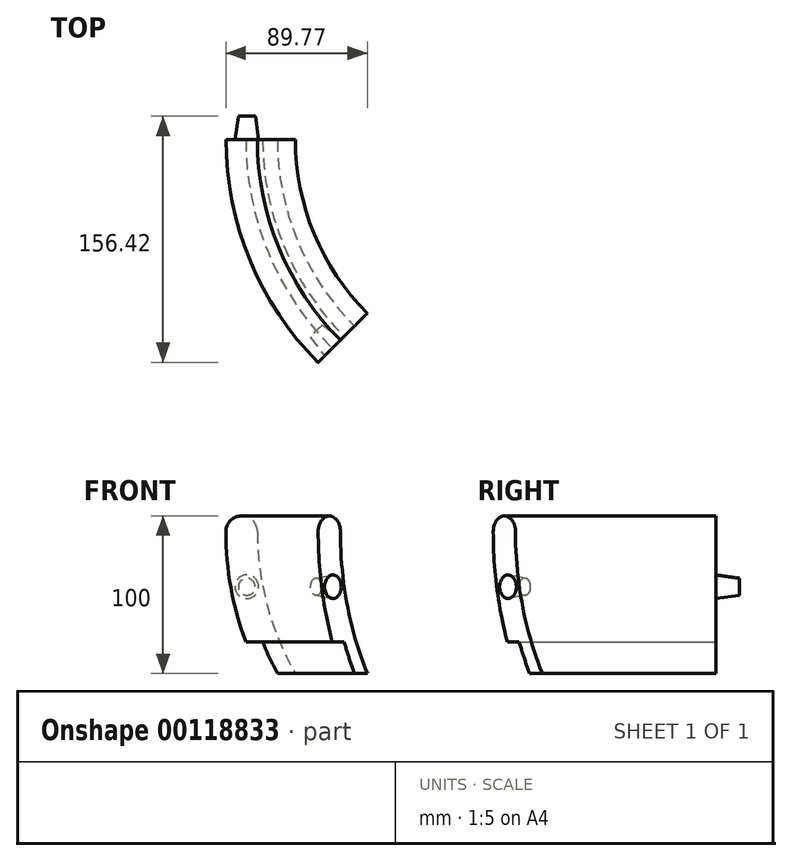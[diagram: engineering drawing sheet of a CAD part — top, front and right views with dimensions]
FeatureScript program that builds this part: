
annotation { "Feature Type Name" : "Feature", "Feature Type Description" : "" }
export const myFeature = defineFeature(function(context is Context, id is Id, definition is map)
    precondition{}
    {
        {
            var Q0;
            Q0=qCreatedBy(makeId("Front.planeOp"),FACE);
            var sketch = newSketch(context, id + "F0", { "sketchPlane" : qUnion([Q0])});
            skArc(sketch, "E0", {"start": v(-72.68, -46.84) * mm, "mid": v(-69.5, -82.4) * mm, "end": v(-60.03, -116.84) * mm});
            skLineSegment(sketch, "E1", {"start": v(127.32, -126.84) * mm, "end": v(127.32, -46.84) * mm});
            skLineSegment(sketch, "E2", {"start": v(127.32, -46.84) * mm, "end": v(-52.68, -46.84) * mm});
            skLineSegment(sketch, "E3", {"start": v(127.32, -126.84) * mm, "end": v(-33.93, -126.84) * mm});
            skLineSegment(sketch, "E4", {"start": v(-60.03, -116.84) * mm, "end": v(-49.31, -116.84) * mm});
            skLineSegment(sketch, "E5", {"start": v(-40.02, -136.84) * mm, "end": v(-28.57, -136.84) * mm});
            skArc(sketch, "E6", {"start": v(-45.02, -126.84) * mm, "mid": v(-42.6, -131.88) * mm, "end": v(-40.02, -136.84) * mm});
            skArc(sketch, "E7", {"start": v(-49.32, -116.84) * mm, "mid": v(-47.24, -121.87) * mm, "end": v(-45.02, -126.84) * mm});
            skArc(sketch, "E8.trimOffspring", {"start": v(-33.93, -126.84) * mm, "mid": v(-31.33, -131.88) * mm, "end": v(-28.57, -136.84) * mm});
            skArc(sketch, "E9", {"start": v(-52.68, -46.84) * mm, "mid": v(-62.68, -36.84) * mm, "end": v(-72.68, -46.84) * mm});
            skSolve(sketch);
        }
        {
            var Q0;
            {var subQ0=sQuery(id+"F0.wireOp",EDGE,"E0");Q0=makeQuery(id+"F0.imprint","IMPRINT",FACE,{"disambiguationData":[TD([[makeQuery(id+"F0.imprint","IMPRINT",EDGE,{"derivedFrom":subQ0}),1.0]])]});}
            var Q1;
            Q1=makeQuery(id+"F0.imprint","IMPRINT",FACE,{"disambiguationData":[TD([[makeQuery(id+"F0.imprint","IMPRINT",EDGE,{"derivedFrom":sQuery(id+"F0.wireOp",EDGE,"njx3f6T8-3ptg-tFr5-qJFg-Vv5jh3EyOicv")}),1.0]])]});
            var Q2;
            Q2=sQuery(id+"F0.wireOp",EDGE,"E1");
            revolve(context, id + "F1", {"entities" : qUnion([Q0, Q1]), "axis" : qUnion([Q2]), "revolveType" : RevolveType.ONE_DIRECTION, "angle" : 45 * degree});
        }
        {
            var Q0;
            Q0=makeQuery(id+"F1.opRevolve","CAP_FACE",FACE,{"disambiguationData":[OSD([sQuery(id+"F0.wireOp",EDGE,"E0"),sQuery(id+"F0.wireOp",EDGE,"E1"),sQuery(id+"F0.wireOp",EDGE,"E2"),sQuery(id+"F0.wireOp",EDGE,"E3"),sQuery(id+"F0.wireOp",EDGE,"E4"),sQuery(id+"F0.wireOp",EDGE,"6592ad9e-64a1-452a-8b5a-3832eb41bc1e"),sQuery(id+"F0.wireOp",EDGE,"957b1381-b19f-4dd3-87c6-36f79a3cc273"),sQuery(id+"F0.wireOp",EDGE,"E5"),sQuery(id+"F0.wireOp",EDGE,"E6"),sQuery(id+"F0.wireOp",EDGE,"E7"),sQuery(id+"F0.wireOp",EDGE,"f6d6ea5c-909c-4789-8fd7-c35fe56b085e"),sQuery(id+"F0.wireOp",EDGE,"9c774b0a-10a6-4efd-b087-42e3d499b3dc.trimOffspring"),sQuery(id+"F0.wireOp",EDGE,"E8.trimOffspring")])],"isStart":false});
            var Q1;
            Q1=makeQuery(id+"F1.opRevolve","CAP_FACE",FACE,{"disambiguationData":[OSD([sQuery(id+"F0.wireOp",EDGE,"E0"),sQuery(id+"F0.wireOp",EDGE,"E1"),sQuery(id+"F0.wireOp",EDGE,"E2"),sQuery(id+"F0.wireOp",EDGE,"E3"),sQuery(id+"F0.wireOp",EDGE,"E4"),sQuery(id+"F0.wireOp",EDGE,"6592ad9e-64a1-452a-8b5a-3832eb41bc1e"),sQuery(id+"F0.wireOp",EDGE,"957b1381-b19f-4dd3-87c6-36f79a3cc273"),sQuery(id+"F0.wireOp",EDGE,"E5"),sQuery(id+"F0.wireOp",EDGE,"E6"),sQuery(id+"F0.wireOp",EDGE,"E7"),sQuery(id+"F0.wireOp",EDGE,"f6d6ea5c-909c-4789-8fd7-c35fe56b085e"),sQuery(id+"F0.wireOp",EDGE,"9c774b0a-10a6-4efd-b087-42e3d499b3dc.trimOffspring"),sQuery(id+"F0.wireOp",EDGE,"E8.trimOffspring")])],"isStart":true});
            var Q2;
            Q2=makeQuery(id+"F1.opRevolve","SWEPT_FACE",FACE,{"disambiguationData":[OSD([sQuery(id+"F0.wireOp",EDGE,"E2")])]});
            var Q3;
            Q3=makeQuery(id+"F1.opRevolve","SWEPT_FACE",FACE,{"disambiguationData":[OSD([sQuery(id+"F0.wireOp",EDGE,"E3")])]});
            var Q4;
            Q4=makeQuery(id+"F1.opRevolve","SWEPT_FACE",FACE,{"disambiguationData":[OSD([sQuery(id+"F0.wireOp",EDGE,"Zm1B8Cns-MwxG-tCiu-5oFE-Pl6dQtbrpGGF")])]});
            var Q5;
            Q5=makeQuery(id+"F1.opRevolve","SWEPT_FACE",FACE,{"disambiguationData":[OSD([sQuery(id+"F0.wireOp",EDGE,"E6"),sQuery(id+"F0.wireOp",EDGE,"E7")])]});
            var Q6;
            Q6=makeQuery(id+"F1.opRevolve","SWEPT_FACE",FACE,{"disambiguationData":[OSD([sQuery(id+"F0.wireOp",EDGE,"E4")])]});
            shell(context, id + "F2", {"entities" : qUnion([Q0, Q1, Q2, Q3, Q4, Q5, Q6]), "thickness" : 20 * mm});
        }
        {
            var Q0;
            Q0=makeQuery(id+"F1.opRevolve","CAP_FACE",FACE,{"disambiguationData":[OSD([sQuery(id+"F0.wireOp",EDGE,"E0"),sQuery(id+"F0.wireOp",EDGE,"E1"),sQuery(id+"F0.wireOp",EDGE,"E2"),sQuery(id+"F0.wireOp",EDGE,"E3"),sQuery(id+"F0.wireOp",EDGE,"E4"),sQuery(id+"F0.wireOp",EDGE,"6592ad9e-64a1-452a-8b5a-3832eb41bc1e"),sQuery(id+"F0.wireOp",EDGE,"957b1381-b19f-4dd3-87c6-36f79a3cc273"),sQuery(id+"F0.wireOp",EDGE,"E5"),sQuery(id+"F0.wireOp",EDGE,"E6"),sQuery(id+"F0.wireOp",EDGE,"E7"),sQuery(id+"F0.wireOp",EDGE,"f6d6ea5c-909c-4789-8fd7-c35fe56b085e"),sQuery(id+"F0.wireOp",EDGE,"9c774b0a-10a6-4efd-b087-42e3d499b3dc.trimOffspring"),sQuery(id+"F0.wireOp",EDGE,"E8.trimOffspring")])],"isStart":false});
            var sketch = newSketch(context, id + "F3", { "sketchPlane" : qUnion([Q0])});
            skCircle(sketch, "E10", {"center": v(-96.72, -81.84) * mm, "radius": 7.5 * mm});
            skSolve(sketch);
        }
        {
            var Q0;
            Q0=qSketchRegion(id+"F3",true);
            extrude(context, id + "F4", {"entities" : qUnion([Q0]), "operationType" : NewBodyOperationType.REMOVE, "oppositeDirection" : true, "depth" : 15 * mm, "hasDraft" : true, "draftAngle" : 8 * degree, "draftPullDirection" : true});
        }
        {
            var Q0;
            Q0=makeQuery(id+"F1.opRevolve","CAP_FACE",FACE,{"disambiguationData":[OSD([sQuery(id+"F0.wireOp",EDGE,"E0"),sQuery(id+"F0.wireOp",EDGE,"E1"),sQuery(id+"F0.wireOp",EDGE,"E2"),sQuery(id+"F0.wireOp",EDGE,"E3"),sQuery(id+"F0.wireOp",EDGE,"E4"),sQuery(id+"F0.wireOp",EDGE,"6592ad9e-64a1-452a-8b5a-3832eb41bc1e"),sQuery(id+"F0.wireOp",EDGE,"957b1381-b19f-4dd3-87c6-36f79a3cc273"),sQuery(id+"F0.wireOp",EDGE,"E5"),sQuery(id+"F0.wireOp",EDGE,"E6"),sQuery(id+"F0.wireOp",EDGE,"E7"),sQuery(id+"F0.wireOp",EDGE,"f6d6ea5c-909c-4789-8fd7-c35fe56b085e"),sQuery(id+"F0.wireOp",EDGE,"9c774b0a-10a6-4efd-b087-42e3d499b3dc.trimOffspring"),sQuery(id+"F0.wireOp",EDGE,"E8.trimOffspring")])],"isStart":true});
            var sketch = newSketch(context, id + "F5", { "sketchPlane" : qUnion([Q0])});
            skCircle(sketch, "E11", {"center": v(59.43, -81.84) * mm, "radius": 7.5 * mm});
            skSolve(sketch);
        }
        {
            var Q0;
            Q0=qSketchRegion(id+"F5",true);
            extrude(context, id + "F6", {"entities" : qUnion([Q0]), "operationType" : NewBodyOperationType.ADD, "depth" : 15 * mm, "hasDraft" : true, "draftAngle" : 8 * degree, "draftPullDirection" : true});
        }
    });
